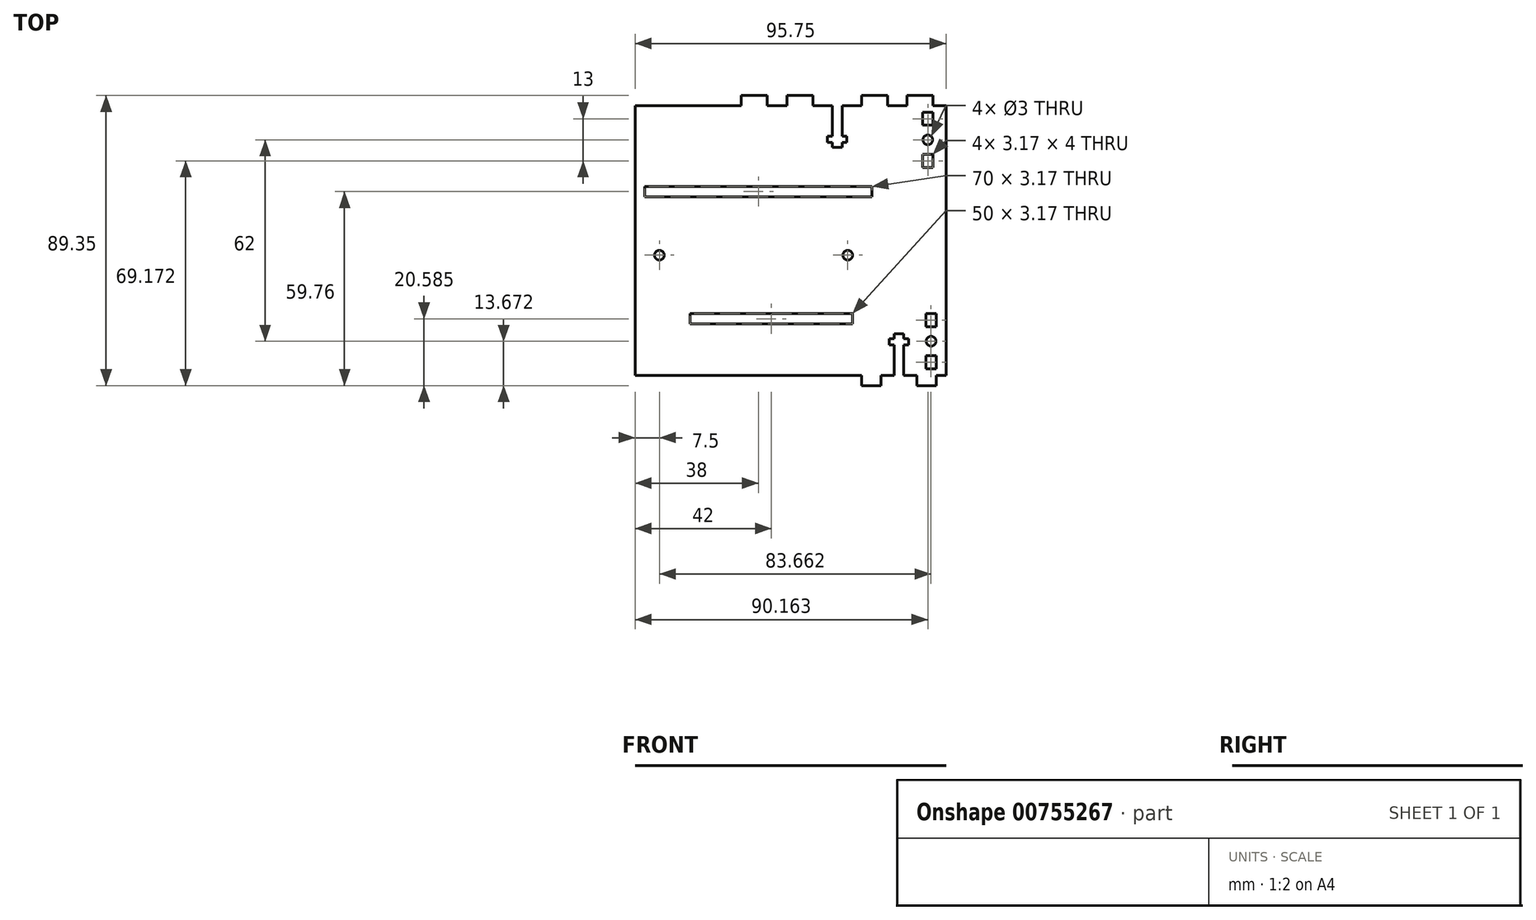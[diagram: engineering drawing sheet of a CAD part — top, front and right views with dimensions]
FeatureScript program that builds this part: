
annotation { "Feature Type Name" : "Feature", "Feature Type Description" : "" }
export const myFeature = defineFeature(function(context is Context, id is Id, definition is map)
    precondition{}
    {
        {
            var Q0;
            Q0=qCreatedBy(makeId("Top.planeOp"),FACE);
            var sketch = newSketch(context, id + "F0", { "sketchPlane" : qUnion([Q0])});
            skLineSegment(sketch, "E0.top", {"start": v(43.2, 27.89) * mm, "end": v(46.2, 27.89) * mm});
            skLineSegment(sketch, "E0.left", {"start": v(43.2, 40.71) * mm, "end": v(43.2, 31.39) * mm});
            skLineSegment(sketch, "E0.right", {"start": v(46.2, 40.71) * mm, "end": v(46.2, 31.39) * mm});
            skPoint(sketch, "E0.middle", {"position": v(44.7, 35.89) * mm});
            skLineSegment(sketch, "E1.bottom", {"start": v(41.7, 31.39) * mm, "end": v(43.2, 31.39) * mm});
            skLineSegment(sketch, "E1.top", {"start": v(41.7, 29.39) * mm, "end": v(43.2, 29.39) * mm});
            skLineSegment(sketch, "E1.left", {"start": v(41.7, 31.39) * mm, "end": v(41.7, 29.39) * mm});
            skLineSegment(sketch, "E1.right", {"start": v(47.7, 31.39) * mm, "end": v(47.7, 29.39) * mm});
            skPoint(sketch, "E1.middle", {"position": v(44.7, 30.39) * mm});
            skLineSegment(sketch, "E2.bottom", {"start": v(52.2, 43.89) * mm, "end": v(60.2, 43.89) * mm});
            skLineSegment(sketch, "E2.left", {"start": v(52.2, 43.89) * mm, "end": v(52.2, 40.71) * mm});
            skLineSegment(sketch, "E2.right", {"start": v(60.2, 43.89) * mm, "end": v(60.2, 40.71) * mm});
            skLineSegment(sketch, "E3.MirrorCS", {"start": v(37.2, 43.89) * mm, "end": v(37.2, 40.71) * mm});
            skLineSegment(sketch, "E4.MirrorCS", {"start": v(37.2, 43.89) * mm, "end": v(29.2, 43.89) * mm});
            skLineSegment(sketch, "E5.MirrorCS", {"start": v(29.2, 43.89) * mm, "end": v(29.2, 40.71) * mm});
            skLineSegment(sketch, "E6", {"start": v(37.2, 40.71) * mm, "end": v(43.2, 40.71) * mm});
            skLineSegment(sketch, "E7.bottom", {"start": v(66.2, 43.89) * mm, "end": v(74.2, 43.89) * mm});
            skLineSegment(sketch, "E7.left", {"start": v(66.2, 43.89) * mm, "end": v(66.2, 40.71) * mm});
            skLineSegment(sketch, "E7.right", {"start": v(74.2, 43.89) * mm, "end": v(74.2, 40.71) * mm});
            skLineSegment(sketch, "E8", {"start": v(60.2, 40.71) * mm, "end": v(66.2, 40.71) * mm});
            skLineSegment(sketch, "E9.MirrorCS", {"start": v(23.2, 43.89) * mm, "end": v(23.2, 40.71) * mm});
            skLineSegment(sketch, "E10.MirrorCS", {"start": v(23.2, 43.89) * mm, "end": v(15.2, 43.89) * mm});
            skLineSegment(sketch, "E11.MirrorCS", {"start": v(15.2, 43.89) * mm, "end": v(15.2, 40.71) * mm});
            skLineSegment(sketch, "E12", {"start": v(23.2, 40.71) * mm, "end": v(29.2, 40.71) * mm});
            skLineSegment(sketch, "E13.bottom", {"start": v(62.2, -29.46) * mm, "end": v(65.2, -29.46) * mm});
            skLineSegment(sketch, "E13.left", {"start": v(62.2, -29.46) * mm, "end": v(62.2, -30.96) * mm});
            skLineSegment(sketch, "E13.right", {"start": v(65.2, -29.46) * mm, "end": v(65.2, -30.96) * mm});
            skPoint(sketch, "E13.middle", {"position": v(63.7, -37.46) * mm});
            skLineSegment(sketch, "E14.bottom", {"start": v(60.7, -30.96) * mm, "end": v(62.2, -30.96) * mm});
            skLineSegment(sketch, "E14.top", {"start": v(60.7, -32.96) * mm, "end": v(62.2, -32.96) * mm});
            skLineSegment(sketch, "E14.left", {"start": v(60.7, -30.96) * mm, "end": v(60.7, -32.96) * mm});
            skLineSegment(sketch, "E14.right", {"start": v(66.7, -30.96) * mm, "end": v(66.7, -32.96) * mm});
            skPoint(sketch, "E14.middle", {"position": v(63.7, -31.96) * mm});
            skLineSegment(sketch, "E15.bottom", {"start": v(69.2, -45.46) * mm, "end": v(75.2, -45.46) * mm});
            skLineSegment(sketch, "E15.left", {"start": v(69.2, -45.46) * mm, "end": v(69.2, -42.29) * mm});
            skLineSegment(sketch, "E15.right", {"start": v(75.2, -45.46) * mm, "end": v(75.2, -42.29) * mm});
            skLineSegment(sketch, "E16.MirrorCS", {"start": v(52.2, -45.46) * mm, "end": v(52.2, -42.29) * mm});
            skLineSegment(sketch, "E17.MirrorCS", {"start": v(58.2, -45.46) * mm, "end": v(52.2, -45.46) * mm});
            skLineSegment(sketch, "E18.MirrorCS", {"start": v(58.2, -45.46) * mm, "end": v(58.2, -42.29) * mm});
            skLineSegment(sketch, "E19", {"start": v(58.2, -42.29) * mm, "end": v(62.2, -42.29) * mm});
            skLineSegment(sketch, "E20.bottom", {"start": v(-14.56, 15.89) * mm, "end": v(55.44, 15.89) * mm});
            skLineSegment(sketch, "E20.top", {"start": v(-14.56, 12.71) * mm, "end": v(55.44, 12.71) * mm});
            skLineSegment(sketch, "E20.left", {"start": v(-14.56, 15.89) * mm, "end": v(-14.56, 12.71) * mm});
            skLineSegment(sketch, "E20.right", {"start": v(55.44, 15.89) * mm, "end": v(55.44, 12.71) * mm});
            skPoint(sketch, "E20.middle", {"position": v(20.44, 14.3) * mm});
            skLineSegment(sketch, "E21.bottom", {"start": v(-0.56, -23.29) * mm, "end": v(49.44, -23.29) * mm});
            skLineSegment(sketch, "E21.top", {"start": v(-0.56, -26.46) * mm, "end": v(49.44, -26.46) * mm});
            skLineSegment(sketch, "E21.left", {"start": v(-0.56, -23.29) * mm, "end": v(-0.56, -26.46) * mm});
            skLineSegment(sketch, "E21.right", {"start": v(49.44, -23.29) * mm, "end": v(49.44, -26.46) * mm});
            skPoint(sketch, "E21.middle", {"position": v(24.44, -24.88) * mm});
            skLineSegment(sketch, "E22", {"start": v(52.2, -42.29) * mm, "end": v(-17.56, -42.29) * mm});
            skLineSegment(sketch, "E23", {"start": v(-17.56, -42.29) * mm, "end": v(-17.56, 40.71) * mm});
            skLineSegment(sketch, "E24", {"start": v(-17.56, 40.71) * mm, "end": v(15.2, 40.71) * mm});
            skCircle(sketch, "E25", {"center": v(72.6, 30.21) * mm, "radius": 1.5 * mm});
            skLineSegment(sketch, "E26.bottom", {"start": v(71.02, 25.71) * mm, "end": v(74.2, 25.71) * mm});
            skLineSegment(sketch, "E26.top", {"start": v(71.02, 21.71) * mm, "end": v(74.2, 21.71) * mm});
            skLineSegment(sketch, "E26.left", {"start": v(71.02, 25.71) * mm, "end": v(71.02, 21.71) * mm});
            skLineSegment(sketch, "E26.right", {"start": v(74.2, 25.71) * mm, "end": v(74.2, 21.71) * mm});
            skPoint(sketch, "E26.middle", {"position": v(72.6, 23.71) * mm});
            skLineSegment(sketch, "E27.MirrorCS", {"start": v(71.02, 34.71) * mm, "end": v(74.2, 34.71) * mm});
            skLineSegment(sketch, "E28.MirrorCS", {"start": v(74.2, 34.71) * mm, "end": v(74.2, 38.71) * mm});
            skLineSegment(sketch, "E29.MirrorCS", {"start": v(71.02, 38.71) * mm, "end": v(74.2, 38.71) * mm});
            skLineSegment(sketch, "E30.MirrorCS", {"start": v(71.02, 34.71) * mm, "end": v(71.02, 38.71) * mm});
            skLineSegment(sketch, "E31", {"start": v(74.2, 40.71) * mm, "end": v(78.2, 40.71) * mm});
            skLineSegment(sketch, "E32", {"start": v(78.2, 40.71) * mm, "end": v(78.2, -42.29) * mm});
            skLineSegment(sketch, "E33", {"start": v(78.2, -42.29) * mm, "end": v(75.2, -42.29) * mm});
            skCircle(sketch, "E34", {"center": v(73.6, -31.79) * mm, "radius": 1.5 * mm});
            skLineSegment(sketch, "E35.bottom", {"start": v(72.02, -36.29) * mm, "end": v(75.2, -36.29) * mm});
            skLineSegment(sketch, "E35.top", {"start": v(72.02, -40.29) * mm, "end": v(75.2, -40.29) * mm});
            skLineSegment(sketch, "E35.left", {"start": v(72.02, -36.29) * mm, "end": v(72.02, -40.29) * mm});
            skLineSegment(sketch, "E35.right", {"start": v(75.2, -36.29) * mm, "end": v(75.2, -40.29) * mm});
            skPoint(sketch, "E35.middle", {"position": v(73.6, -38.29) * mm});
            skLineSegment(sketch, "E36.MirrorCS", {"start": v(72.02, -27.29) * mm, "end": v(75.2, -27.29) * mm});
            skLineSegment(sketch, "E37.MirrorCS", {"start": v(72.02, -27.29) * mm, "end": v(72.02, -23.29) * mm});
            skLineSegment(sketch, "E38.MirrorCS", {"start": v(75.2, -27.29) * mm, "end": v(75.2, -23.29) * mm});
            skLineSegment(sketch, "E39.MirrorCS", {"start": v(72.02, -23.29) * mm, "end": v(75.2, -23.29) * mm});
            skCircle(sketch, "E40", {"center": v(-10.06, -5.29) * mm, "radius": 1.5 * mm});
            skPoint(sketch, "E40.centerSnap0", {"position": v(36.96, -5.29) * mm});
            skCircle(sketch, "E41", {"center": v(47.94, -5.29) * mm, "radius": 1.5 * mm});
            skPoint(sketch, "E42.MirrorCS.start.orphan", {"position": v(23.2, 40.71) * mm});
            skPoint(sketch, "E43.MirrorCS.end.orphan", {"position": v(29.2, 40.71) * mm});
            skPoint(sketch, "E43.MirrorCS.start.orphan", {"position": v(37.2, 40.71) * mm});
            skLineSegment(sketch, "E44.trimOffspring", {"start": v(46.2, 40.71) * mm, "end": v(52.2, 40.71) * mm});
            skPoint(sketch, "E0.bottom.end.orphan", {"position": v(46.2, 43.89) * mm});
            skPoint(sketch, "E0.bottom.start.orphan", {"position": v(43.2, 43.89) * mm});
            skLineSegment(sketch, "E45.trimOffspring", {"start": v(46.2, 31.39) * mm, "end": v(47.7, 31.39) * mm});
            skLineSegment(sketch, "E46.trimOffspring", {"start": v(46.2, 29.39) * mm, "end": v(46.2, 27.89) * mm});
            skLineSegment(sketch, "E47.trimOffspring", {"start": v(46.2, 29.39) * mm, "end": v(47.7, 29.39) * mm});
            skLineSegment(sketch, "E48.trimOffspring", {"start": v(43.2, 29.39) * mm, "end": v(43.2, 27.89) * mm});
            skPoint(sketch, "E49.end.orphan", {"position": v(20.44, 15.89) * mm});
            skPoint(sketch, "E50.end.orphan", {"position": v(-14.56, 14.3) * mm});
            skPoint(sketch, "E51.orphan", {"position": v(36.96, 12.71) * mm});
            skPoint(sketch, "E52.end.orphan", {"position": v(36.96, -23.29) * mm});
            skPoint(sketch, "E53.end.orphan", {"position": v(-0.56, -24.88) * mm});
            skPoint(sketch, "E13.top.end.orphan", {"position": v(65.2, -45.46) * mm});
            skPoint(sketch, "E54.orphan", {"position": v(62.2, -45.46) * mm});
            skLineSegment(sketch, "E55.trimOffspring", {"start": v(65.2, -42.29) * mm, "end": v(69.2, -42.29) * mm});
            skLineSegment(sketch, "E56.trimOffspring", {"start": v(65.2, -32.96) * mm, "end": v(66.7, -32.96) * mm});
            skLineSegment(sketch, "E57.trimOffspring", {"start": v(62.2, -32.96) * mm, "end": v(62.2, -42.29) * mm});
            skLineSegment(sketch, "E58.trimOffspring", {"start": v(65.2, -30.96) * mm, "end": v(66.7, -30.96) * mm});
            skLineSegment(sketch, "E59.trimOffspring", {"start": v(65.2, -32.96) * mm, "end": v(65.2, -42.29) * mm});
            skSolve(sketch);
        }
        {
            var Q0;
            {var subQ19=sQuery(id+"F0.wireOp",EDGE,"E0.top");Q0=makeQuery(id+"F0.imprint","IMPRINT",FACE,{"disambiguationData":[TD([[makeQuery(id+"F0.imprint","IMPRINT",EDGE,{"derivedFrom":subQ19}),-1.0]])]});}
            var Q1;
            Q1=makeQuery(id+"F0.imprint","IMPRINT",FACE,{"disambiguationData":[TD([[makeQuery(id+"F0.imprint","IMPRINT",EDGE,{"derivedFrom":sQuery(id+"F0.wireOp",EDGE,"E3.MirrorCS")}),-1.0]])]});
            var Q2;
            Q2=makeQuery(id+"F0.imprint","IMPRINT",FACE,{"disambiguationData":[TD([[makeQuery(id+"F0.imprint","IMPRINT",EDGE,{"derivedFrom":sQuery(id+"F0.wireOp",EDGE,"E9.MirrorCS")}),-1.0]])]});
            var Q3;
            Q3=makeQuery(id+"F0.imprint","IMPRINT",FACE,{"disambiguationData":[TD([[makeQuery(id+"F0.imprint","IMPRINT",EDGE,{"derivedFrom":sQuery(id+"F0.wireOp",EDGE,"E2.bottom")}),-1.0]])]});
            var Q4;
            Q4=makeQuery(id+"F0.imprint","IMPRINT",FACE,{"disambiguationData":[TD([[makeQuery(id+"F0.imprint","IMPRINT",EDGE,{"derivedFrom":sQuery(id+"F0.wireOp",EDGE,"E7.bottom")}),-1.0]])]});
            var Q5;
            Q5=makeQuery(id+"F0.imprint","IMPRINT",FACE,{"disambiguationData":[TD([[makeQuery(id+"F0.imprint","IMPRINT",EDGE,{"derivedFrom":sQuery(id+"F0.wireOp",EDGE,"E15.bottom")}),1.0]])]});
            var Q6;
            Q6=makeQuery(id+"F0.imprint","IMPRINT",FACE,{"disambiguationData":[TD([[makeQuery(id+"F0.imprint","IMPRINT",EDGE,{"derivedFrom":sQuery(id+"F0.wireOp",EDGE,"1e311aa6-722d-44d9-a490-a69c3547eded0.MirrorCS")}),1.0]])]});
            extrude(context, id + "F1", {"entities" : qUnion([Q0, Q1, Q2, Q3, Q4, Q5, Q6]), "depth" : 1 / 203.2 * mm, "offsetDistance" : 25 * mm});
        }
    });
